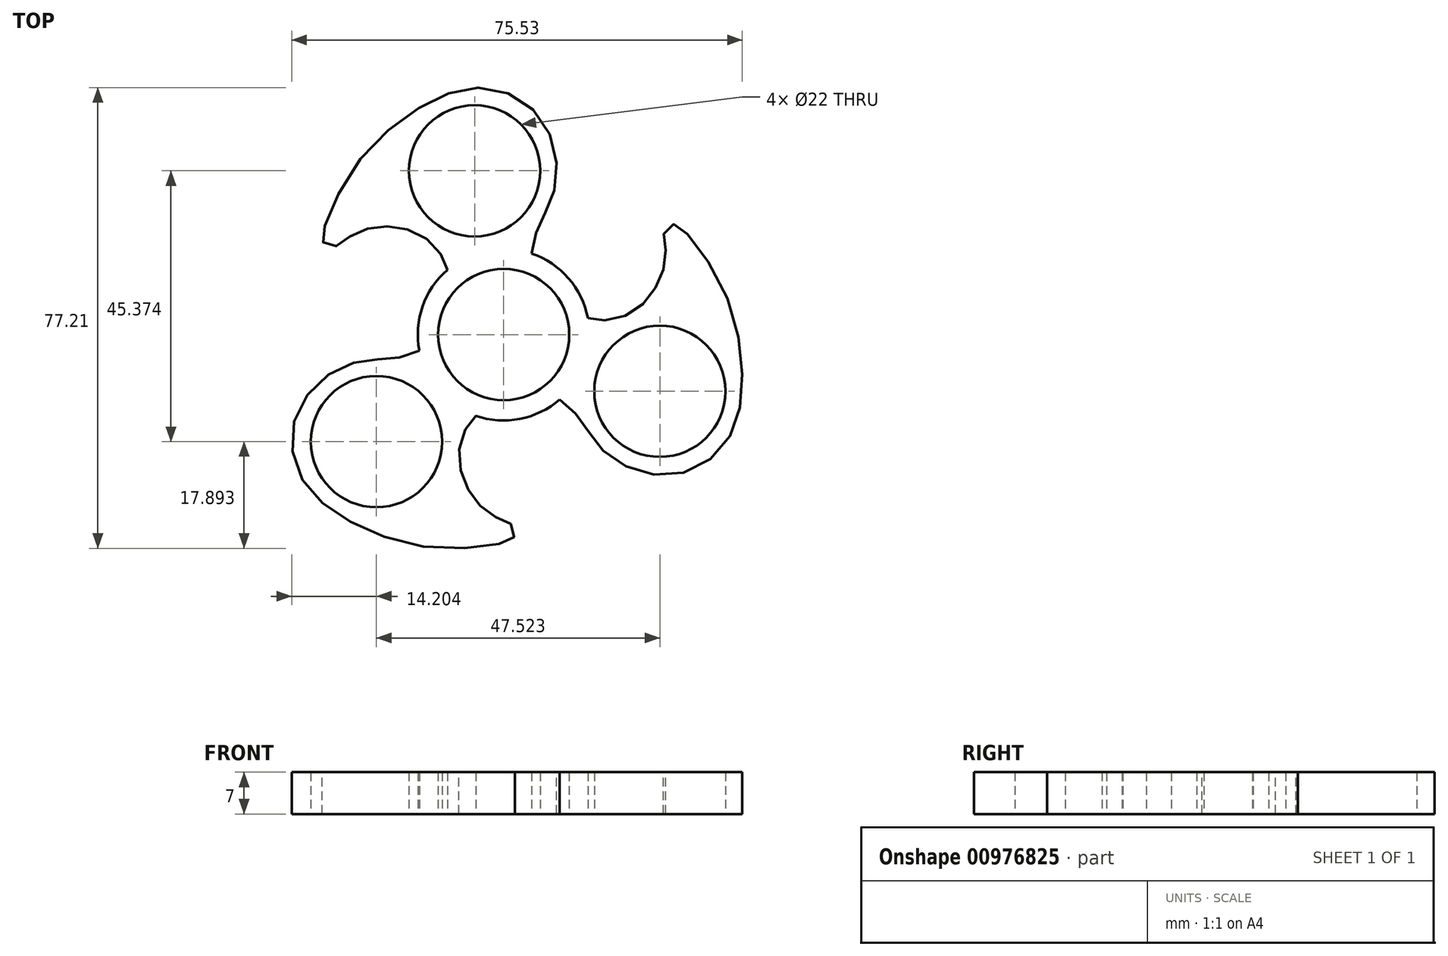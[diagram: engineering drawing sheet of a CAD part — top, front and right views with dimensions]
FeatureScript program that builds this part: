
annotation { "Feature Type Name" : "Feature", "Feature Type Description" : "" }
export const myFeature = defineFeature(function(context is Context, id is Id, definition is map)
    precondition{}
    {
        {
            var Q0;
            Q0=qCreatedBy(makeId("Top.planeOp"),FACE);
            var sketch = newSketch(context, id + "F0", { "sketchPlane" : qUnion([Q0])});
            skCircle(sketch, "E0", {"center": v(0, 0) * mm, "radius": 11 * mm});
            skCircle(sketch, "E1", {"center": v(0, 0) * mm, "radius": 14.38 * mm});
            skCircle(sketch, "E2", {"center": v(26.2, -9.5) * mm, "radius": 11 * mm});
            skFitSpline(sketch, "E3", {"points": [v(14.12, 2.74) * mm, v(17.08, 2.4) * mm, v(21.4, 3.67) * mm, v(24.72, 6.73) * mm, v(26.63, 10.3) * mm, v(27.14, 14.11) * mm, v(26.88, 16.91) * mm, v(28.28, 18.44) * mm, v(29.81, 17.8) * mm, v(36.94, 7.36) * mm, v(40, -7.54) * mm, v(37.84, -17.22) * mm, v(30.83, -22.95) * mm, v(22.04, -22.7) * mm, v(15.8, -18.5) * mm, v(12.75, -14.03) * mm, v(9.41, -10.87) * mm], "startDerivative": vector(61.61, -13.13) * mm, "endDerivative": vector(-63.4, 51.48) * mm});
            skSolve(sketch);
        }
        {
            var Q0;
            Q0=qSketchRegion(id+"F0",true);
            extrude(context, id + "F1", {"entities" : qUnion([Q0]), "depth" : 7 * mm, "offsetDistance" : 25 * mm});
        }
        {
            var Q0;
            Q0=makeQuery(id+"F1.opExtrude","SWEPT_BODY",BODY,{"disambiguationData":[OSD([sQuery(id+"F0.wireOp",EDGE,"E0"),sQuery(id+"F0.wireOp",EDGE,"E1"),sQuery(id+"F0.wireOp",EDGE,"E2"),sQuery(id+"F0.wireOp",EDGE,"E3")])]});
            var Q1;
            Q1=makeQuery(id+"F1.opExtrude","CAP_EDGE",EDGE,{"disambiguationData":[OSD([sQuery(id+"F0.wireOp",EDGE,"E0")])],"isStart":true});
            circularPattern(context, id + "F2", {"operationType" : NewBodyOperationType.ADD, "entities" : qUnion([Q0]), "axis" : qUnion([Q1]), "angle" : 360 * degree, "instanceCount" : 3, "equalSpace" : true});
        }
    });
